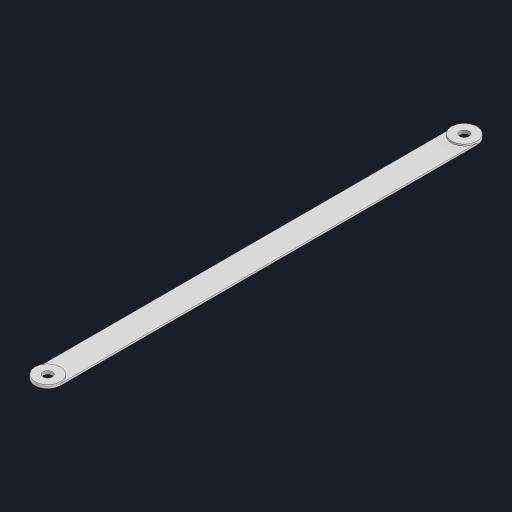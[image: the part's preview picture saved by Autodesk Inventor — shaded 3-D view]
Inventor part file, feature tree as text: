
AUTODESK INVENTOR PART (.ipt)
format: ipt  version: 2023 (Build 270158000, 158)  size: 95,744 bytes
history: native  units: mm
features: extrude x2, sketch x1
ambient origin geometry x8: Origin, YZ Plane, XZ Plane, XY Plane, X Axis, Y Axis, Z Axis, Center Point
bodies: Body1 (feature_tree)
feature tree (3):
  sketch  "Sketch1"  dims[d0=5.5mm d1=15.0mm d14=5.5mm d15=15.0mm d16=1.0mm d17=0.0mm d18=2.0mm d19=0.0mm d20=259.423mm]
  extrude  "Extrusion4"  Depth=15.0mm
  extrude  "Extrusion5"  Depth=2.0mm
